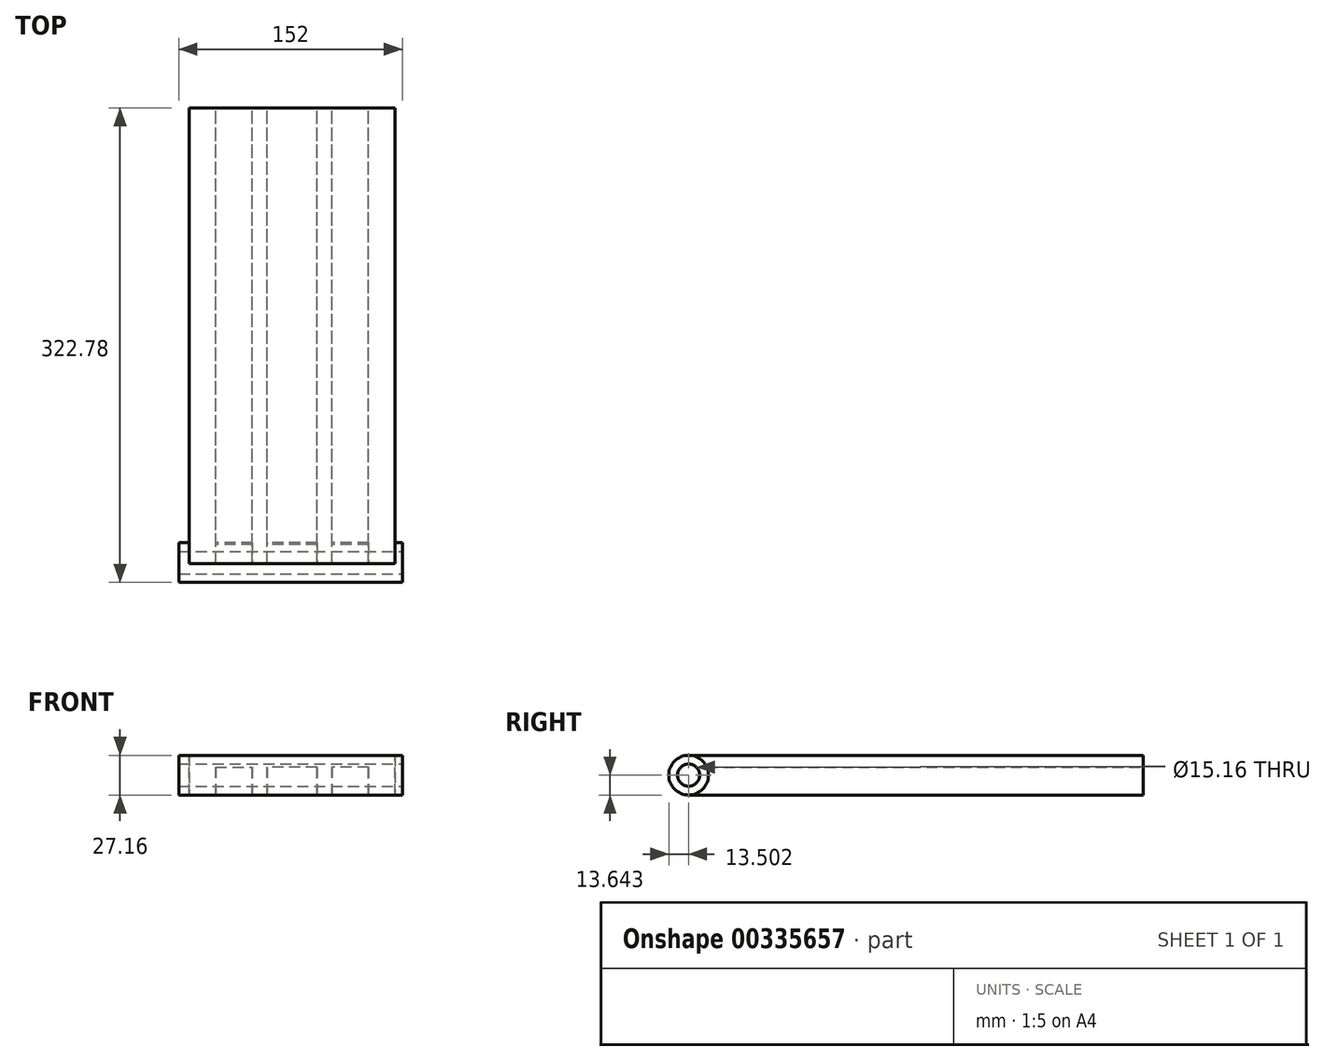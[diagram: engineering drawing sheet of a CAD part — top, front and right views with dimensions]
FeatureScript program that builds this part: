
annotation { "Feature Type Name" : "Feature", "Feature Type Description" : "" }
export const myFeature = defineFeature(function(context is Context, id is Id, definition is map)
    precondition{}
    {
        {
            var Q0;
            Q0=qCreatedBy(makeId("Front.planeOp"),FACE);
            var sketch = newSketch(context, id + "F0", { "sketchPlane" : qUnion([Q0])});
            skLineSegment(sketch, "E0.top", {"start": v(-51.02, -19.16) * mm, "end": v(-69.02, -19.16) * mm});
            skLineSegment(sketch, "E0.left", {"start": v(-51.02, 0) * mm, "end": v(-51.02, -19.16) * mm});
            skLineSegment(sketch, "E0.right", {"start": v(-69.02, 3.84) * mm, "end": v(-69.02, -19.16) * mm});
            skLineSegment(sketch, "E1.top", {"start": v(52.98, -19.16) * mm, "end": v(70.98, -19.16) * mm});
            skLineSegment(sketch, "E1.left", {"start": v(52.98, 0) * mm, "end": v(52.98, -19.16) * mm});
            skLineSegment(sketch, "E1.right", {"start": v(70.98, 3.84) * mm, "end": v(70.98, -19.16) * mm});
            skLineSegment(sketch, "E2.bottom", {"start": v(17.98, 0) * mm, "end": v(-16.02, 0) * mm});
            skLineSegment(sketch, "E3.top", {"start": v(-69.02, 8) * mm, "end": v(70.98, 8) * mm});
            skLineSegment(sketch, "E3.left", {"start": v(-69.02, 3.84) * mm, "end": v(-69.02, 8) * mm});
            skLineSegment(sketch, "E3.right", {"start": v(70.98, 3.84) * mm, "end": v(70.98, 8) * mm});
            skLineSegment(sketch, "E4.0", {"start": v(-26.02, 0) * mm, "end": v(-26.02, -19.16) * mm});
            skLineSegment(sketch, "E5.0", {"start": v(27.98, 0) * mm, "end": v(27.98, -19.16) * mm});
            skLineSegment(sketch, "E6.0", {"start": v(-16.02, 0) * mm, "end": v(-16.02, -19.16) * mm});
            skLineSegment(sketch, "E7.0", {"start": v(17.98, 0) * mm, "end": v(17.98, -19.16) * mm});
            skLineSegment(sketch, "E8", {"start": v(-16.02, -19.16) * mm, "end": v(-26.02, -19.16) * mm});
            skLineSegment(sketch, "E9", {"start": v(17.98, -19.16) * mm, "end": v(27.98, -19.16) * mm});
            skLineSegment(sketch, "E10", {"start": v(52.98, 0) * mm, "end": v(27.98, 0) * mm});
            skLineSegment(sketch, "E11", {"start": v(-51.02, 0) * mm, "end": v(-26.02, 0) * mm});
            skLineSegment(sketch, "E12", {"start": v(-51.02, 0) * mm, "end": v(-51.02, 8) * mm});
            skLineSegment(sketch, "E13", {"start": v(52.98, 0) * mm, "end": v(52.98, 8) * mm});
            skLineSegment(sketch, "E14", {"start": v(-26.02, 0) * mm, "end": v(-26.02, 8) * mm});
            skLineSegment(sketch, "E15", {"start": v(-16.02, 0) * mm, "end": v(-16.02, 8) * mm});
            skLineSegment(sketch, "E16", {"start": v(17.98, 0) * mm, "end": v(17.98, 8) * mm});
            skLineSegment(sketch, "E17", {"start": v(27.98, 0) * mm, "end": v(27.98, 8) * mm});
            skSolve(sketch);
        }
        {
            var Q0;
            Q0=makeQuery(id+"F0.imprint","IMPRINT",FACE,{"disambiguationData":[TD([[makeQuery(id+"F0.imprint","IMPRINT",EDGE,{"derivedFrom":sQuery(id+"F0.wireOp",EDGE,"E1.top")}),1.0]])]});
            var Q1;
            Q1=makeQuery(id+"F0.imprint","IMPRINT",FACE,{"disambiguationData":[TD([[makeQuery(id+"F0.imprint","IMPRINT",EDGE,{"derivedFrom":sQuery(id+"F0.wireOp",EDGE,"E0.top")}),-1.0]])]});
            extrude(context, id + "F1", {"entities" : qUnion([Q0, Q1]), "depth" : 310 * mm});
        }
        {
            var Q0;
            Q0=makeQuery(id+"F0.imprint","IMPRINT",FACE,{"disambiguationData":[TD([[makeQuery(id+"F0.imprint","IMPRINT",EDGE,{"derivedFrom":sQuery(id+"F0.wireOp",EDGE,"E2.bottom")}),-1.0]])]});
            extrude(context, id + "F2", {"entities" : qUnion([Q0]), "depth" : 250 * mm});
        }
        {
            var Q0;
            Q0=makeQuery(id+"F0.imprint","IMPRINT",FACE,{"disambiguationData":[TD([[makeQuery(id+"F0.imprint","IMPRINT",EDGE,{"derivedFrom":sQuery(id+"F0.wireOp",EDGE,"E4.0")}),1.0]])]});
            var Q1;
            Q1=makeQuery(id+"F0.imprint","IMPRINT",FACE,{"disambiguationData":[TD([[makeQuery(id+"F0.imprint","IMPRINT",EDGE,{"derivedFrom":sQuery(id+"F0.wireOp",EDGE,"E5.0")}),-1.0]])]});
            extrude(context, id + "F3", {"entities" : qUnion([Q0, Q1]), "operationType" : NewBodyOperationType.ADD, "depth" : 310 * mm});
        }
        {
            var Q0;
            Q0=makeQuery(id+"F0.imprint","IMPRINT",FACE,{"disambiguationData":[TD([[makeQuery(id+"F0.imprint","IMPRINT",EDGE,{"derivedFrom":sQuery(id+"F0.wireOp",EDGE,"E11")}),1.0]])]});
            var Q1;
            Q1=makeQuery(id+"F0.imprint","IMPRINT",FACE,{"disambiguationData":[TD([[makeQuery(id+"F0.imprint","IMPRINT",EDGE,{"derivedFrom":sQuery(id+"F0.wireOp",EDGE,"E10")}),-1.0]])]});
            var Q2;
            Q2=makeQuery(id+"F0.imprint","IMPRINT",FACE,{"disambiguationData":[TD([[makeQuery(id+"F0.imprint","IMPRINT",EDGE,{"derivedFrom":sQuery(id+"F0.wireOp",EDGE,"E2.bottom")}),-1.0]])]});
            extrude(context, id + "F4", {"entities" : qUnion([Q0, Q1, Q2]), "depth" : 309.9 * mm});
        }
        {
            var Q0;
            Q0=qCreatedBy(makeId("Right.planeOp"),FACE);
            var sketch = newSketch(context, id + "F5", { "sketchPlane" : qUnion([Q0])});
            skCircle(sketch, "E18", {"center": v(-309.28, -5.52) * mm, "radius": 13.5 * mm});
            skPoint(sketch, "E18.first.point", {"position": v(-310.03, 7.96) * mm});
            skPoint(sketch, "E18.second.point", {"position": v(-309.92, -19) * mm});
            skPoint(sketch, "E18.third.point", {"position": v(-313.11, -18.46) * mm});
            skSolve(sketch);
        }
        {
            var Q0;
            Q0=makeQuery(id+"F5.imprint","IMPRINT",FACE,{"disambiguationData":[TD([[makeQuery(id+"F5.imprint","IMPRINT",EDGE,{"derivedFrom":sQuery(id+"F5.wireOp",EDGE,"E18")}),1.0]])]});
            extrude(context, id + "F6", {"entities" : qUnion([Q0]), "operationType" : NewBodyOperationType.ADD, "endBound" : BoundingType.SYMMETRIC, "depth" : 152 * mm});
        }
        {
            var Q0;
            Q0=makeQuery(id+"F6.opExtrude","CAP_FACE",FACE,{"disambiguationData":[OSD([sQuery(id+"F5.wireOp",EDGE,"E18")])],"isStart":false});
            var sketch = newSketch(context, id + "F7", { "sketchPlane" : qUnion([Q0])});
            skCircle(sketch, "E19", {"center": v(-309.28, -5.52) * mm, "radius": 7.58 * mm});
            skSolve(sketch);
        }
        {
            var Q0;
            Q0=makeQuery(id+"F7.imprint","IMPRINT",FACE,{"disambiguationData":[TD([[makeQuery(id+"F7.imprint","IMPRINT",EDGE,{"derivedFrom":sQuery(id+"F7.wireOp",EDGE,"E19")}),1.0]])]});
            extrude(context, id + "F8", {"entities" : qUnion([Q0]), "operationType" : NewBodyOperationType.REMOVE, "oppositeDirection" : true, "depth" : 325 * mm});
        }
    });
